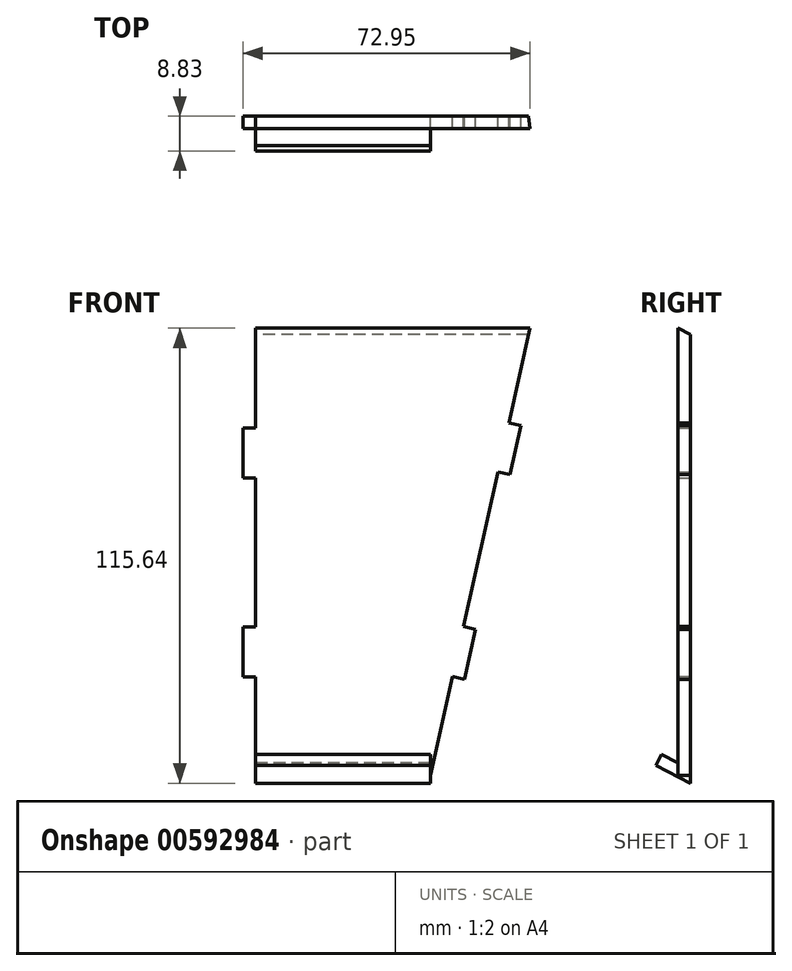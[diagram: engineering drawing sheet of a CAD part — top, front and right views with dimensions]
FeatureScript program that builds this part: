
annotation { "Feature Type Name" : "Feature", "Feature Type Description" : "" }
export const myFeature = defineFeature(function(context is Context, id is Id, definition is map)
    precondition{}
    {
        {
            var Q0;
            Q0=qCreatedBy(makeId("Front.planeOp"),FACE);
            var sketch = newSketch(context, id + "F0", { "sketchPlane" : qUnion([Q0])});
            skLineSegment(sketch, "E0.bottom", {"start": v(9.45, -57.01) * mm, "end": v(-34.92, -57.01) * mm});
            skLineSegment(sketch, "E0.top", {"start": v(34.85, 57.01) * mm, "end": v(-34.92, 57.01) * mm});
            skLineSegment(sketch, "E0.right", {"start": v(-38.1, -31.61) * mm, "end": v(-38.1, -18.91) * mm});
            skPoint(sketch, "E0.middle", {"position": v(0, 0) * mm});
            skLineSegment(sketch, "E1", {"start": v(-34.92, -57.01) * mm, "end": v(9.45, -57.01) * mm});
            skLineSegment(sketch, "E2", {"start": v(18.22, -32.22) * mm, "end": v(21.05, -19.52) * mm});
            skPoint(sketch, "E3.orphan", {"position": v(38.1, -57.01) * mm});
            skLineSegment(sketch, "E4", {"start": v(-34.92, 57.01) * mm, "end": v(-34.92, 31.61) * mm});
            skLineSegment(sketch, "E5", {"start": v(-34.92, 31.61) * mm, "end": v(-38.1, 31.61) * mm});
            skLineSegment(sketch, "E6", {"start": v(-38.1, 31.61) * mm, "end": v(-38.1, 18.91) * mm});
            skLineSegment(sketch, "E7", {"start": v(-38.1, 18.91) * mm, "end": v(-34.93, 18.91) * mm});
            skLineSegment(sketch, "E8", {"start": v(-34.93, 18.91) * mm, "end": v(-34.92, -18.91) * mm});
            skLineSegment(sketch, "E9", {"start": v(-34.92, -18.91) * mm, "end": v(-38.1, -18.91) * mm});
            skLineSegment(sketch, "E10", {"start": v(-38.1, -18.91) * mm, "end": v(-38.1, -31.61) * mm});
            skLineSegment(sketch, "E11", {"start": v(-38.1, -31.61) * mm, "end": v(-34.92, -31.61) * mm});
            skLineSegment(sketch, "E12", {"start": v(-34.92, -31.61) * mm, "end": v(-34.92, -57.01) * mm});
            skPoint(sketch, "E13.orphan", {"position": v(-38.1, 57.01) * mm});
            skLineSegment(sketch, "E14.trimOffspring", {"start": v(-38.1, 18.91) * mm, "end": v(-38.1, 31.61) * mm});
            skPoint(sketch, "E15.orphan", {"position": v(-38.1, -57.01) * mm});
            skLineSegment(sketch, "E16", {"start": v(21.05, -19.52) * mm, "end": v(17.95, -18.83) * mm});
            skLineSegment(sketch, "E17", {"start": v(17.95, -18.83) * mm, "end": v(26.72, 20.51) * mm});
            skLineSegment(sketch, "E18", {"start": v(26.72, 20.51) * mm, "end": v(29.82, 19.82) * mm});
            skLineSegment(sketch, "E19", {"start": v(29.82, 19.82) * mm, "end": v(32.58, 32.22) * mm});
            skLineSegment(sketch, "E20", {"start": v(32.58, 32.22) * mm, "end": v(29.48, 32.9) * mm});
            skLineSegment(sketch, "E21", {"start": v(29.48, 32.9) * mm, "end": v(34.85, 57.01) * mm});
            skPoint(sketch, "E22.end.orphan", {"position": v(9.45, -57.01) * mm});
            skPoint(sketch, "E23.end.orphan", {"position": v(12.7, -42.4) * mm});
            skLineSegment(sketch, "E24", {"start": v(18.22, -32.22) * mm, "end": v(15.12, -31.53) * mm});
            skLineSegment(sketch, "E25", {"start": v(15.12, -31.53) * mm, "end": v(9.45, -57.01) * mm});
            skPoint(sketch, "E26.orphan", {"position": v(38.1, 57.01) * mm});
            skPoint(sketch, "E27.end.orphan", {"position": v(15.8, -43.1) * mm});
            skPoint(sketch, "E28.orphan", {"position": v(12.7, -57.01) * mm});
            skSolve(sketch);
        }
        {
            var Q0;
            Q0 = qSketchRegion(id + "F0", true);
            extrude(context, id + "F1", {"entities" : qUnion([Q0]), "depth" : 3.17 * mm, "offsetDistance" : 25.4 * mm});
        }
        {
            var Q0;
            Q0=makeQuery(id+"F1.opExtrude","SWEPT_FACE",FACE,{"disambiguationData":[OSD([sQuery(id+"F0.wireOp",EDGE,"E12")])]});
            var sketch = newSketch(context, id + "F2", { "sketchPlane" : qUnion([Q0])});
            skLineSegment(sketch, "E29", {"start": v(3.17, -57.01) * mm, "end": v(8.83, -54.13) * mm});
            skLineSegment(sketch, "E30", {"start": v(8.83, -54.13) * mm, "end": v(7.4, -51.3) * mm});
            skLineSegment(sketch, "E31", {"start": v(7.4, -51.3) * mm, "end": v(0, -55.06) * mm});
            skLineSegment(sketch, "E32", {"start": v(0, -55.06) * mm, "end": v(0, -58.63) * mm});
            skLineSegment(sketch, "E33", {"start": v(3.17, -57.01) * mm, "end": v(0, -58.63) * mm});
            skSolve(sketch);
        }
        {
            var Q0;
            Q0 = qSketchRegion(id + "F2", true);
            var Q1;
            {var subQ0=sQuery(id+"F2.wireOp",EDGE,"gtquZHyb-BIPY-AWKI-ODDM-ETVRPOuQAGwS");Q1=makeQuery(id+"F2.imprint","IMPRINT",FACE,{"disambiguationData":[TD([[makeQuery(id+"F2.imprint","IMPRINT",EDGE,{"derivedFrom":subQ0}),1.0]])]});}
            extrude(context, id + "F3", {"entities" : qUnion([Q0, Q1]), "operationType" : NewBodyOperationType.ADD, "oppositeDirection" : true, "depth" : 43.94 * mm, "offsetDistance" : 25.4 * mm});
        }
        {
            var Q0;
            Q0=makeQuery(id+"F1.opExtrude","SWEPT_FACE",FACE,{"disambiguationData":[OSD([sQuery(id+"F0.wireOp",EDGE,"E4")])]});
            var sketch = newSketch(context, id + "F4", { "sketchPlane" : qUnion([Q0])});
            skLineSegment(sketch, "E34", {"start": v(3.18, 57.01) * mm, "end": v(-2.5, 54.12) * mm});
            skLineSegment(sketch, "E35", {"start": v(3.18, 57.01) * mm, "end": v(0, 57.01) * mm});
            skLineSegment(sketch, "E36", {"start": v(0, 57.01) * mm, "end": v(0, 55.4) * mm});
            skSolve(sketch);
        }
        {
            var Q0;
            {var subQ0=sQuery(id+"F4.wireOp",EDGE,"E35");Q0=makeQuery(id+"F4.imprint","IMPRINT",FACE,{"disambiguationData":[TD([[makeQuery(id+"F4.imprint","IMPRINT",EDGE,{"derivedFrom":subQ0}),1.0]])]});}
            extrude(context, id + "F5", {"entities" : qUnion([Q0]), "operationType" : NewBodyOperationType.REMOVE, "oppositeDirection" : true, "depth" : 76.2 * mm, "offsetDistance" : 25.4 * mm});
        }
        {
            var Q0;
            Q0 = qSketchRegion(id + "F2", true);
            extrude(context, id + "F6", {"entities" : qUnion([Q0]), "operationType" : NewBodyOperationType.ADD, "oppositeDirection" : true, "depth" : 44.45 * mm, "offsetDistance" : 25.4 * mm});
        }
    });
